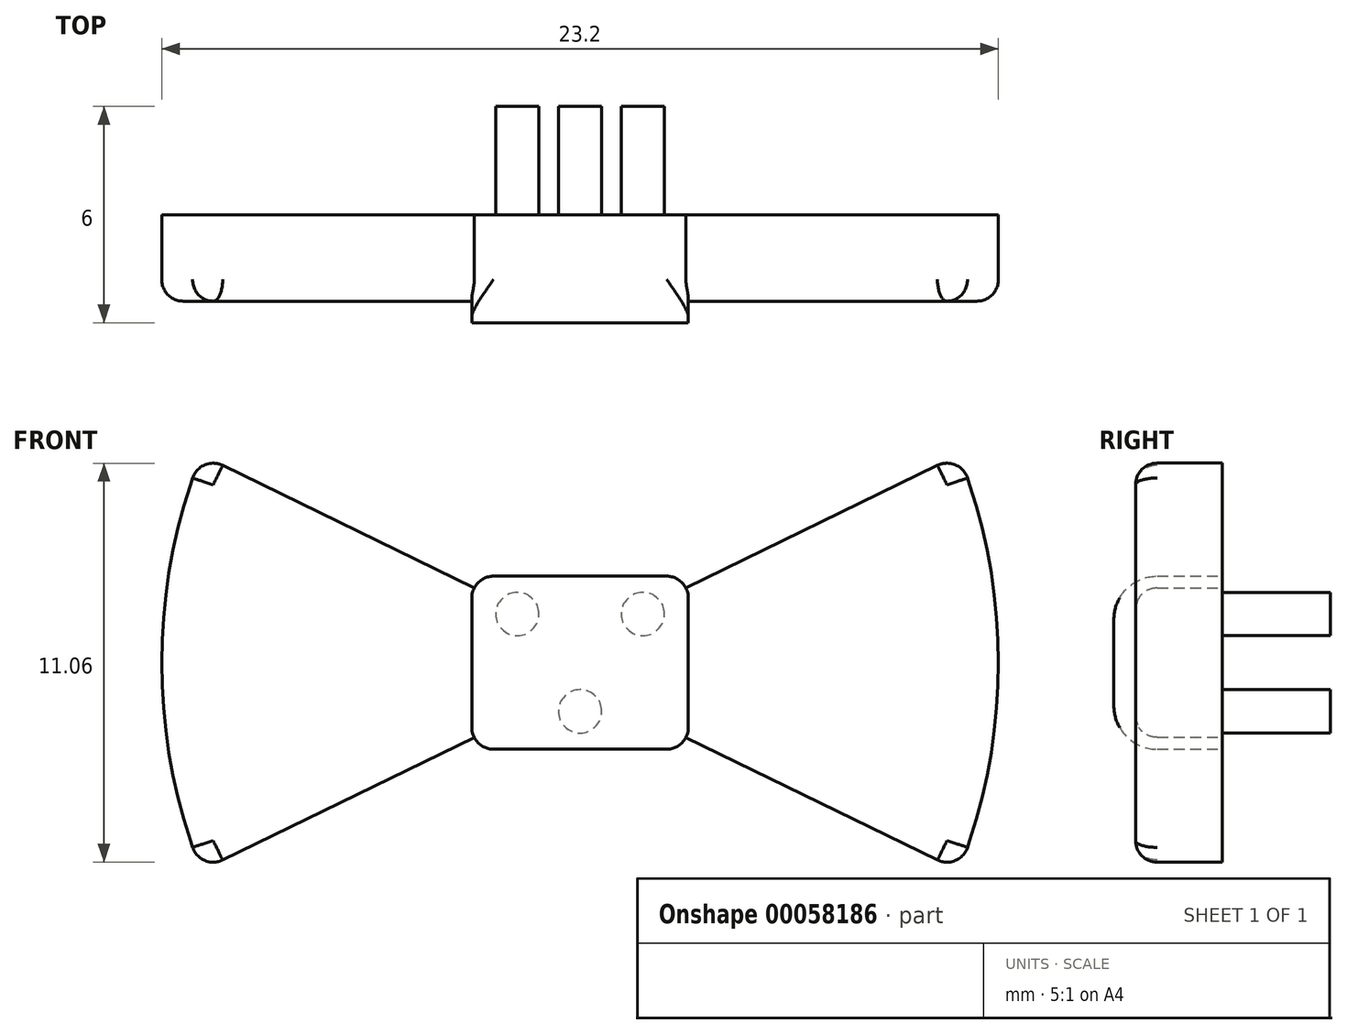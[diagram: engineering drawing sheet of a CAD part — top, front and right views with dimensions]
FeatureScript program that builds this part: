
annotation { "Feature Type Name" : "Feature", "Feature Type Description" : "" }
export const myFeature = defineFeature(function(context is Context, id is Id, definition is map)
    precondition{}
    {
        {
            var Q0;
            Q0=qCreatedBy(makeId("Front.planeOp"),FACE);
            var sketch = newSketch(context, id + "F0", { "sketchPlane" : qUnion([Q0])});
            skLineSegment(sketch, "E0.bottom", {"start": v(-4, 4) * mm, "end": v(4, 4) * mm});
            skLineSegment(sketch, "E0.top", {"start": v(-4, -4) * mm, "end": v(4, -4) * mm});
            skLineSegment(sketch, "E0.left", {"start": v(-5, 3) * mm, "end": v(-5, -3) * mm});
            skLineSegment(sketch, "E0.right", {"start": v(5, 3) * mm, "end": v(5, -3) * mm});
            skPoint(sketch, "E1.visualSharp", {"position": v(-5, 4) * mm});
            skArc(sketch, "E1.filletArc", {"start": v(-4, 4) * mm, "mid": v(-4.7, 3.7) * mm, "end": v(-5, 3) * mm});
            skPoint(sketch, "E2.visualSharp", {"position": v(-5, -4) * mm});
            skArc(sketch, "E2.filletArc", {"start": v(-5, -3) * mm, "mid": v(-4.7, -3.7) * mm, "end": v(-4, -4) * mm});
            skPoint(sketch, "E3.visualSharp", {"position": v(5, -4) * mm});
            skArc(sketch, "E3.filletArc", {"start": v(4, -4) * mm, "mid": v(4.7, -3.7) * mm, "end": v(5, -3) * mm});
            skPoint(sketch, "E4.visualSharp", {"position": v(5, 4) * mm});
            skArc(sketch, "E4.filletArc", {"start": v(5, 3) * mm, "mid": v(4.7, 3.7) * mm, "end": v(4, 4) * mm});
            skPoint(sketch, "E5.visualSharp", {"position": v(-18, 9.91) * mm});
            skArc(sketch, "E5.filletArc", {"start": v(-17.8, 8.85) * mm, "mid": v(-17.95, 8.56) * mm, "end": v(-18, 8.25) * mm});
            skPoint(sketch, "E6.visualSharp", {"position": v(-18, -9.91) * mm});
            skArc(sketch, "E6.filletArc", {"start": v(-18, -8.25) * mm, "mid": v(-17.95, -8.56) * mm, "end": v(-17.8, -8.85) * mm});
            skLineSegment(sketch, "E7", {"start": v(-4.9, 3.45) * mm, "end": v(-16.53, 9.13) * mm});
            skLineSegment(sketch, "E8", {"start": v(-4.9, -3.45) * mm, "end": v(-16.53, -9.13) * mm});
            skLineSegment(sketch, "E9.MirrorCS", {"start": v(4.9, 3.45) * mm, "end": v(16.53, 9.13) * mm});
            skLineSegment(sketch, "E10.MirrorCS", {"start": v(4.9, -3.45) * mm, "end": v(16.53, -9.13) * mm});
            skArc(sketch, "E11", {"start": v(-18, 8.25) * mm, "mid": v(-19.33, 0) * mm, "end": v(-18, -8.25) * mm});
            skArc(sketch, "E12.MirrorCS", {"start": v(18, 8.25) * mm, "mid": v(19.33, 0) * mm, "end": v(18, -8.25) * mm});
            skPoint(sketch, "E13.MirrorCS.end.orphan", {"position": v(18, -8.25) * mm});
            skPoint(sketch, "E13.MirrorCS.start.orphan", {"position": v(18, 8.25) * mm});
            skLineSegment(sketch, "E14", {"start": v(-16.53, 9.13) * mm, "end": v(-17.53, 9.66) * mm});
            skLineSegment(sketch, "E15", {"start": v(-16.53, -9.13) * mm, "end": v(-17.53, -9.66) * mm});
            skLineSegment(sketch, "E16", {"start": v(-18, 8.25) * mm, "end": v(-17.53, 9.66) * mm});
            skLineSegment(sketch, "E17", {"start": v(-18, -8.25) * mm, "end": v(-17.53, -9.66) * mm});
            skPoint(sketch, "E18.MirrorCS.end.orphan", {"position": v(16.53, -9.13) * mm});
            skPoint(sketch, "E19.MirrorCS.start.orphan", {"position": v(16.53, 9.13) * mm});
            skLineSegment(sketch, "E20.MirrorCS", {"start": v(18, -8.25) * mm, "end": v(17.53, -9.66) * mm});
            skLineSegment(sketch, "E21.MirrorCS", {"start": v(16.53, -9.13) * mm, "end": v(17.53, -9.66) * mm});
            skLineSegment(sketch, "E22.MirrorCS", {"start": v(16.53, 9.13) * mm, "end": v(17.53, 9.66) * mm});
            skLineSegment(sketch, "E23.MirrorCS", {"start": v(18, 8.25) * mm, "end": v(17.53, 9.66) * mm});
            skLineSegment(sketch, "E24.rect.bottom", {"start": v(-2.9, 2.25) * mm, "end": v(2.9, 2.25) * mm});
            skLineSegment(sketch, "E24.rect.top", {"start": v(-2.9, -2.25) * mm, "end": v(2.9, -2.25) * mm});
            skLineSegment(sketch, "E24.rect.left", {"start": v(-2.9, 2.25) * mm, "end": v(-2.9, -2.25) * mm});
            skLineSegment(sketch, "E24.rect.right", {"start": v(2.9, 2.25) * mm, "end": v(2.9, -2.25) * mm});
            skPoint(sketch, "E24.rect.middle", {"position": v(0, 0) * mm});
            skCircle(sketch, "E25", {"center": v(-2.9, 2.25) * mm, "radius": 1 * mm});
            skCircle(sketch, "E26", {"center": v(2.9, 2.25) * mm, "radius": 1 * mm});
            skCircle(sketch, "E27", {"center": v(0, -2.25) * mm, "radius": 1 * mm});
            skSolve(sketch);
        }
        {
            var Q0;
            {var subQ3=sQuery(id+"F0.wireOp",EDGE,"E0.bottom");Q0=makeQuery(id+"F0.imprint","IMPRINT",FACE,{"disambiguationData":[TD([[makeQuery(id+"F0.imprint","IMPRINT",EDGE,{"derivedFrom":subQ3}),-1.0]])]});}
            var Q1;
            {var subQ0=sQuery(id+"F0.wireOp",EDGE,"E24.rect.left");var subQ1=sQuery(id+"F0.wireOp",EDGE,"E24.rect.bottom");var subQ2=makeQuery(id+"F0.imprint","INTERSECT",VERTEX,{"derivedFrom":[subQ1,subQ0]});Q1=makeQuery(id+"F0.imprint","IMPRINT",FACE,{"disambiguationData":[TD([[makeQuery(id+"F0.imprint","IMPRINT",EDGE,{"disambiguationData":[TD([[subQ2,-1.0]])],"derivedFrom":subQ1}),1.0]])]});}
            var Q2;
            {var subQ0=sQuery(id+"F0.wireOp",EDGE,"E24.rect.left");var subQ1=sQuery(id+"F0.wireOp",EDGE,"E24.rect.bottom");var subQ2=makeQuery(id+"F0.imprint","INTERSECT",VERTEX,{"derivedFrom":[subQ1,subQ0]});Q2=makeQuery(id+"F0.imprint","IMPRINT",FACE,{"disambiguationData":[TD([[makeQuery(id+"F0.imprint","IMPRINT",EDGE,{"disambiguationData":[TD([[subQ2,-1.0]])],"derivedFrom":subQ1}),-1.0]])]});}
            var Q3;
            {var subQ3=sQuery(id+"F0.wireOp",EDGE,"E25");var subQ5=sQuery(id+"F0.wireOp",EDGE,"E24.rect.bottom");var subQ6=makeQuery(id+"F0.imprint","INTERSECT",VERTEX,{"derivedFrom":[subQ5,subQ3]});Q3=makeQuery(id+"F0.imprint","IMPRINT",FACE,{"disambiguationData":[TD([[makeQuery(id+"F0.imprint","IMPRINT",EDGE,{"disambiguationData":[TD([[subQ6,-1.0]])],"derivedFrom":subQ5}),-1.0]])]});}
            var Q4;
            {var subQ0=sQuery(id+"F0.wireOp",EDGE,"E24.rect.right");var subQ1=sQuery(id+"F0.wireOp",EDGE,"E24.rect.bottom");var subQ2=makeQuery(id+"F0.imprint","INTERSECT",VERTEX,{"derivedFrom":[subQ1,subQ0]});Q4=makeQuery(id+"F0.imprint","IMPRINT",FACE,{"disambiguationData":[TD([[makeQuery(id+"F0.imprint","IMPRINT",EDGE,{"disambiguationData":[TD([[subQ2,1.0]])],"derivedFrom":subQ1}),-1.0]])]});}
            var Q5;
            {var subQ0=sQuery(id+"F0.wireOp",EDGE,"E24.rect.right");var subQ1=sQuery(id+"F0.wireOp",EDGE,"E24.rect.bottom");var subQ2=makeQuery(id+"F0.imprint","INTERSECT",VERTEX,{"derivedFrom":[subQ1,subQ0]});Q5=makeQuery(id+"F0.imprint","IMPRINT",FACE,{"disambiguationData":[TD([[makeQuery(id+"F0.imprint","IMPRINT",EDGE,{"disambiguationData":[TD([[subQ2,1.0]])],"derivedFrom":subQ1}),1.0]])]});}
            var Q6;
            {var subQ0=sQuery(id+"F0.wireOp",EDGE,"E27");var subQ1=sQuery(id+"F0.wireOp",EDGE,"E24.rect.top");var subQ2=makeQuery(id+"F0.imprint","INTERSECT",VERTEX,{"disambiguationData":[OD(0.0)],"derivedFrom":[subQ1,subQ0]});Q6=makeQuery(id+"F0.imprint","IMPRINT",FACE,{"disambiguationData":[TD([[makeQuery(id+"F0.imprint","IMPRINT",EDGE,{"disambiguationData":[TD([[subQ2,-1.0]])],"derivedFrom":subQ1}),1.0]])]});}
            var Q7;
            {var subQ0=sQuery(id+"F0.wireOp",EDGE,"E27");var subQ1=sQuery(id+"F0.wireOp",EDGE,"E24.rect.top");var subQ2=makeQuery(id+"F0.imprint","INTERSECT",VERTEX,{"disambiguationData":[OD(0.0)],"derivedFrom":[subQ1,subQ0]});Q7=makeQuery(id+"F0.imprint","IMPRINT",FACE,{"disambiguationData":[TD([[makeQuery(id+"F0.imprint","IMPRINT",EDGE,{"disambiguationData":[TD([[subQ2,-1.0]])],"derivedFrom":subQ1}),-1.0]])]});}
            extrude(context, id + "F1", {"entities" : qUnion([Q0, Q1, Q2, Q3, Q4, Q5, Q6, Q7]), "depth" : 5 * mm});
        }
        {
            var Q0;
            {var subQ1=sQuery(id+"F0.wireOp",EDGE,"E0.left");Q0=makeQuery(id+"F0.imprint","IMPRINT",FACE,{"disambiguationData":[TD([[makeQuery(id+"F0.imprint","IMPRINT",EDGE,{"derivedFrom":subQ1}),-1.0]])]});}
            var Q1;
            {var subQ1=sQuery(id+"F0.wireOp",EDGE,"E0.right");Q1=makeQuery(id+"F0.imprint","IMPRINT",FACE,{"disambiguationData":[TD([[makeQuery(id+"F0.imprint","IMPRINT",EDGE,{"derivedFrom":subQ1}),1.0]])]});}
            extrude(context, id + "F2", {"entities" : qUnion([Q0, Q1]), "operationType" : NewBodyOperationType.ADD, "depth" : 4 * mm});
        }
        {
            var Q0;
            Q0=makeQuery(id+"F1.opExtrude","CAP_EDGE",EDGE,{"disambiguationData":[OSD([sQuery(id+"F0.wireOp",EDGE,"E0.bottom")])],"isStart":false});
            var Q1;
            Q1=makeQuery(id+"F1.opExtrude","CAP_EDGE",EDGE,{"disambiguationData":[OSD([sQuery(id+"F0.wireOp",EDGE,"E0.top")])],"isStart":false});
            fillet(context, id + "F3", {"entities" : qUnion([Q0, Q1]), "radius" : 2 * mm, "allowEdgeOverflow" : false});
        }
        {
            var Q0;
            Q0=makeQuery(id+"F2.opExtrude","SWEPT_EDGE",EDGE,{"disambiguationData":[OSD([sQuery(id+"F0.wireOp",EDGE,"E14"),sQuery(id+"F0.wireOp",EDGE,"E16")])]});
            var Q1;
            Q1=makeQuery(id+"F2.opExtrude","SWEPT_EDGE",EDGE,{"disambiguationData":[OSD([sQuery(id+"F0.wireOp",EDGE,"E15"),sQuery(id+"F0.wireOp",EDGE,"E17")])]});
            var Q2;
            Q2=makeQuery(id+"F2.opExtrude","SWEPT_EDGE",EDGE,{"disambiguationData":[OSD([sQuery(id+"F0.wireOp",EDGE,"E20.MirrorCS"),sQuery(id+"F0.wireOp",EDGE,"E21.MirrorCS")])]});
            var Q3;
            Q3=makeQuery(id+"F2.opExtrude","SWEPT_EDGE",EDGE,{"disambiguationData":[OSD([sQuery(id+"F0.wireOp",EDGE,"E22.MirrorCS"),sQuery(id+"F0.wireOp",EDGE,"E23.MirrorCS")])]});
            var Q4;
            Q4=makeQuery(id+"F2.opExtrude","CAP_EDGE",EDGE,{"disambiguationData":[OSD([sQuery(id+"F0.wireOp",EDGE,"E7")])],"isStart":false});
            var Q5;
            Q5=makeQuery(id+"F2.opExtrude","CAP_EDGE",EDGE,{"disambiguationData":[OSD([sQuery(id+"F0.wireOp",EDGE,"E8")])],"isStart":false});
            var Q6;
            Q6=makeQuery(id+"F2.opExtrude","CAP_EDGE",EDGE,{"disambiguationData":[OSD([sQuery(id+"F0.wireOp",EDGE,"E10.MirrorCS")])],"isStart":false});
            var Q7;
            Q7=makeQuery(id+"F2.opExtrude","CAP_EDGE",EDGE,{"disambiguationData":[OSD([sQuery(id+"F0.wireOp",EDGE,"E9.MirrorCS")])],"isStart":false});
            fillet(context, id + "F4", {"entities" : qUnion([Q0, Q1, Q2, Q3, Q4, Q5, Q6, Q7]), "radius" : 1 * mm, "tangentPropagation" : true, "allowEdgeOverflow" : false});
        }
        {
            var Q0;
            Q0=makeQuery(id+"F2.opExtrude","CAP_EDGE",EDGE,{"disambiguationData":[OSD([sQuery(id+"F0.wireOp",EDGE,"E11")])],"isStart":false});
            var Q1;
            Q1=makeQuery(id+"F2.opExtrude","CAP_EDGE",EDGE,{"disambiguationData":[OSD([sQuery(id+"F0.wireOp",EDGE,"E12.MirrorCS")])],"isStart":false});
            fillet(context, id + "F5", {"entities" : qUnion([Q0, Q1]), "radius" : 1 * mm, "tangentPropagation" : true, "allowEdgeOverflow" : false});
        }
        {
            var Q0;
            {var subQ0=sQuery(id+"F0.wireOp",EDGE,"E24.rect.right");var subQ1=sQuery(id+"F0.wireOp",EDGE,"E24.rect.bottom");var subQ2=makeQuery(id+"F0.imprint","INTERSECT",VERTEX,{"derivedFrom":[subQ1,subQ0]});Q0=makeQuery(id+"F0.imprint","IMPRINT",FACE,{"disambiguationData":[TD([[makeQuery(id+"F0.imprint","IMPRINT",EDGE,{"disambiguationData":[TD([[subQ2,1.0]])],"derivedFrom":subQ1}),1.0]])]});}
            var Q1;
            {var subQ0=sQuery(id+"F0.wireOp",EDGE,"E24.rect.left");var subQ1=sQuery(id+"F0.wireOp",EDGE,"E24.rect.bottom");var subQ2=makeQuery(id+"F0.imprint","INTERSECT",VERTEX,{"derivedFrom":[subQ1,subQ0]});Q1=makeQuery(id+"F0.imprint","IMPRINT",FACE,{"disambiguationData":[TD([[makeQuery(id+"F0.imprint","IMPRINT",EDGE,{"disambiguationData":[TD([[subQ2,-1.0]])],"derivedFrom":subQ1}),-1.0]])]});}
            var Q2;
            {var subQ0=sQuery(id+"F0.wireOp",EDGE,"E24.rect.left");var subQ1=sQuery(id+"F0.wireOp",EDGE,"E24.rect.bottom");var subQ2=makeQuery(id+"F0.imprint","INTERSECT",VERTEX,{"derivedFrom":[subQ1,subQ0]});Q2=makeQuery(id+"F0.imprint","IMPRINT",FACE,{"disambiguationData":[TD([[makeQuery(id+"F0.imprint","IMPRINT",EDGE,{"disambiguationData":[TD([[subQ2,-1.0]])],"derivedFrom":subQ1}),1.0]])]});}
            var Q3;
            {var subQ0=sQuery(id+"F0.wireOp",EDGE,"E27");var subQ1=sQuery(id+"F0.wireOp",EDGE,"E24.rect.top");var subQ2=makeQuery(id+"F0.imprint","INTERSECT",VERTEX,{"disambiguationData":[OD(0.0)],"derivedFrom":[subQ1,subQ0]});Q3=makeQuery(id+"F0.imprint","IMPRINT",FACE,{"disambiguationData":[TD([[makeQuery(id+"F0.imprint","IMPRINT",EDGE,{"disambiguationData":[TD([[subQ2,-1.0]])],"derivedFrom":subQ1}),1.0]])]});}
            var Q4;
            {var subQ0=sQuery(id+"F0.wireOp",EDGE,"E24.rect.right");var subQ1=sQuery(id+"F0.wireOp",EDGE,"E24.rect.bottom");var subQ2=makeQuery(id+"F0.imprint","INTERSECT",VERTEX,{"derivedFrom":[subQ1,subQ0]});Q4=makeQuery(id+"F0.imprint","IMPRINT",FACE,{"disambiguationData":[TD([[makeQuery(id+"F0.imprint","IMPRINT",EDGE,{"disambiguationData":[TD([[subQ2,1.0]])],"derivedFrom":subQ1}),-1.0]])]});}
            var Q5;
            {var subQ0=sQuery(id+"F0.wireOp",EDGE,"E27");var subQ1=sQuery(id+"F0.wireOp",EDGE,"E24.rect.top");var subQ2=makeQuery(id+"F0.imprint","INTERSECT",VERTEX,{"disambiguationData":[OD(0.0)],"derivedFrom":[subQ1,subQ0]});Q5=makeQuery(id+"F0.imprint","IMPRINT",FACE,{"disambiguationData":[TD([[makeQuery(id+"F0.imprint","IMPRINT",EDGE,{"disambiguationData":[TD([[subQ2,-1.0]])],"derivedFrom":subQ1}),-1.0]])]});}
            var Q6;
            Q6=sQuery(id+"F0.wireOp",EDGE,"E27");
            var Q7;
            Q7=sQuery(id+"F0.wireOp",EDGE,"E26");
            var Q8;
            Q8=sQuery(id+"F0.wireOp",EDGE,"E25");
            extrude(context, id + "F6", {"entities" : qUnion([Q0, Q1, Q2, Q3, Q4, Q5]), "operationType" : NewBodyOperationType.ADD, "surfaceEntities" : qUnion([Q6, Q7, Q8]), "oppositeDirection" : true, "depth" : 5 * mm});
        }
        {
            var Q0;
            Q0=makeQuery(id+"F1.opExtrude","SWEPT_BODY",BODY,{"disambiguationData":[OSD([sQuery(id+"F0.wireOp",EDGE,"E0.bottom"),sQuery(id+"F0.wireOp",EDGE,"E0.top"),sQuery(id+"F0.wireOp",EDGE,"E0.left"),sQuery(id+"F0.wireOp",EDGE,"E0.right"),sQuery(id+"F0.wireOp",EDGE,"E1.filletArc"),sQuery(id+"F0.wireOp",EDGE,"E2.filletArc"),sQuery(id+"F0.wireOp",EDGE,"E3.filletArc"),sQuery(id+"F0.wireOp",EDGE,"E4.filletArc")])]});
            var Q1;
            Q1=qCreatedBy(makeId("Origin.pointOp"),VERTEX);
            transform(context, id + "F7", {"entities" : qUnion([Q0]), "transformType" : TransformType.SCALE_UNIFORMLY, "scale" : .6, "scalePoint" : qUnion([Q1]), "makeCopy" : false});
        }
    });
